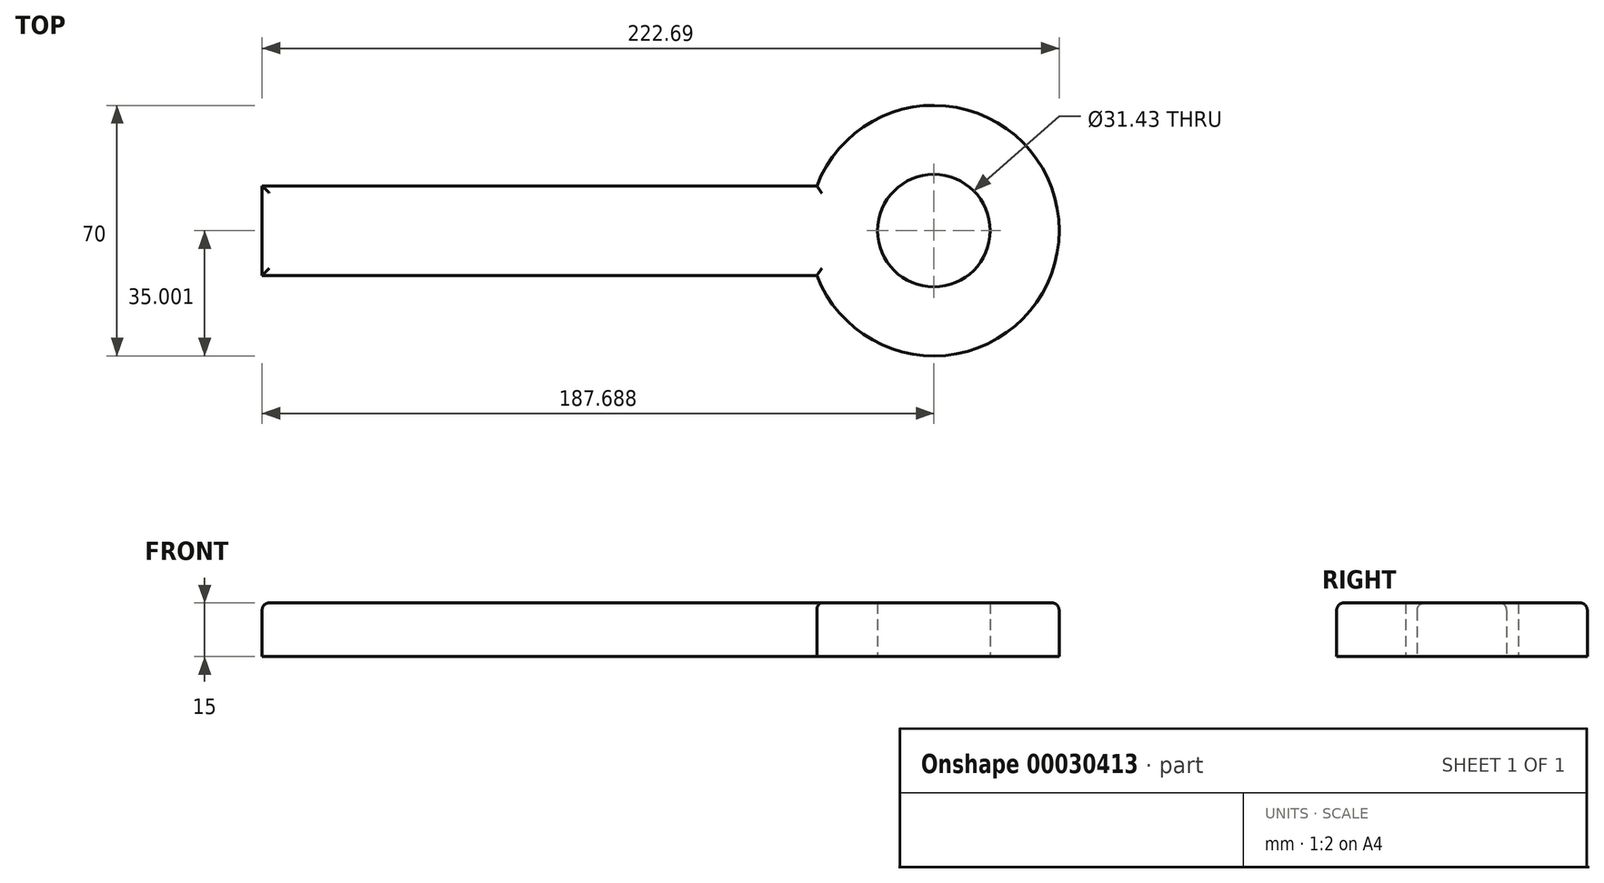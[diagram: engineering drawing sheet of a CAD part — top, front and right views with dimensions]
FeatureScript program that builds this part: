
annotation { "Feature Type Name" : "Feature", "Feature Type Description" : "" }
export const myFeature = defineFeature(function(context is Context, id is Id, definition is map)
    precondition{}
    {
        {
            var Q0;
            Q0=qCreatedBy(makeId("Top.planeOp"),FACE);
            var sketch = newSketch(context, id + "F0", { "sketchPlane" : qUnion([Q0])});
            skLineSegment(sketch, "E0.bottom", {"start": v(-82.43, 22.24) * mm, "end": v(72.57, 22.24) * mm});
            skLineSegment(sketch, "E0.top", {"start": v(-82.43, -2.76) * mm, "end": v(72.57, -2.76) * mm});
            skLineSegment(sketch, "E0.left", {"start": v(-82.43, 22.24) * mm, "end": v(-82.43, -2.76) * mm});
            skLineSegment(sketch, "E0.right", {"start": v(72.57, 22.24) * mm, "end": v(72.57, -2.76) * mm});
            skLineSegment(sketch, "E1.bottom", {"start": v(-82.43, -2.76) * mm, "end": v(-72.43, -2.76) * mm});
            skLineSegment(sketch, "E1.top", {"start": v(-82.43, -32.76) * mm, "end": v(-72.43, -32.76) * mm});
            skLineSegment(sketch, "E1.left", {"start": v(-82.43, -2.76) * mm, "end": v(-82.43, -32.76) * mm});
            skLineSegment(sketch, "E1.right", {"start": v(-72.43, -2.76) * mm, "end": v(-72.43, -32.76) * mm});
            skLineSegment(sketch, "E2.bottom", {"start": v(-62.43, -2.76) * mm, "end": v(-54.43, -2.76) * mm});
            skLineSegment(sketch, "E2.top", {"start": v(-62.43, -17.76) * mm, "end": v(-54.43, -17.76) * mm});
            skLineSegment(sketch, "E2.left", {"start": v(-62.43, -2.76) * mm, "end": v(-62.43, -17.76) * mm});
            skLineSegment(sketch, "E2.right", {"start": v(-54.43, -2.76) * mm, "end": v(-54.43, -17.76) * mm});
            skLineSegment(sketch, "E3", {"start": v(-44.43, -2.76) * mm, "end": v(-30.43, -2.76) * mm});
            skLineSegment(sketch, "E4", {"start": v(-30.43, -2.76) * mm, "end": v(-37.43, -16.03) * mm});
            skLineSegment(sketch, "E5", {"start": v(-44.43, -2.76) * mm, "end": v(-37.43, -16.03) * mm});
            skArc(sketch, "E6", {"start": v(72.57, -2.76) * mm, "mid": v(140.26, 9.74) * mm, "end": v(72.57, 22.24) * mm});
            skCircle(sketch, "E7", {"center": v(105.26, 9.74) * mm, "radius": 15.71 * mm});
            skLineSegment(sketch, "E8", {"start": v(-82.43, 9.74) * mm, "end": v(105.26, 9.74) * mm, "construction": true});
            skSolve(sketch);
        }
        {
            var Q0;
            Q0=makeQuery(id+"F0.imprint","IMPRINT",FACE,{"disambiguationData":[TD([[makeQuery(id+"F0.imprint","IMPRINT",EDGE,{"derivedFrom":sQuery(id+"F0.wireOp",EDGE,"E0.bottom")}),-1.0]])]});
            var Q1;
            Q1=makeQuery(id+"F0.imprint","IMPRINT",FACE,{"disambiguationData":[TD([[makeQuery(id+"F0.imprint","IMPRINT",EDGE,{"derivedFrom":sQuery(id+"F0.wireOp",EDGE,"E1.bottom")}),-1.0]])]});
            var Q2;
            Q2=makeQuery(id+"F0.imprint","IMPRINT",FACE,{"disambiguationData":[TD([[makeQuery(id+"F0.imprint","IMPRINT",EDGE,{"derivedFrom":sQuery(id+"F0.wireOp",EDGE,"E2.bottom")}),-1.0]])]});
            var Q3;
            Q3=makeQuery(id+"F0.imprint","IMPRINT",FACE,{"disambiguationData":[TD([[makeQuery(id+"F0.imprint","IMPRINT",EDGE,{"derivedFrom":sQuery(id+"F0.wireOp",EDGE,"E3")}),-1.0]])]});
            var Q4;
            Q4=makeQuery(id+"F0.imprint","IMPRINT",FACE,{"disambiguationData":[TD([[makeQuery(id+"F0.imprint","IMPRINT",EDGE,{"derivedFrom":sQuery(id+"F0.wireOp",EDGE,"E0.right")}),1.0]])]});
            extrude(context, id + "F1", {"entities" : qUnion([Q0, Q1, Q2, Q3, Q4]), "depth" : 15 * mm});
        }
        {
            var Q0;
            Q0=makeQuery(id+"F1.opExtrude","CAP_EDGE",EDGE,{"disambiguationData":[OSD([sQuery(id+"F0.wireOp",EDGE,"E0.left"),sQuery(id+"F0.wireOp",EDGE,"E1.left")])],"isStart":false});
            var Q1;
            Q1=makeQuery(id+"F1.opExtrude","CAP_EDGE",EDGE,{"disambiguationData":[OSD([sQuery(id+"F0.wireOp",EDGE,"E0.bottom")])],"isStart":false});
            var Q2;
            Q2=makeQuery(id+"F1.opExtrude","CAP_EDGE",EDGE,{"disambiguationData":[OSD([sQuery(id+"F0.wireOp",EDGE,"E1.right")])],"isStart":false});
            var Q3;
            Q3=makeQuery(id+"F1.opExtrude","CAP_EDGE",EDGE,{"disambiguationData":[OSD([sQuery(id+"F0.wireOp",EDGE,"E1.top")])],"isStart":false});
            var Q4;
            {var subQ0=sQuery(id+"F0.wireOp",EDGE,"E0.top");Q4=makeQuery(id+"F1.opExtrude","CAP_EDGE",EDGE,{"disambiguationData":[OSD([subQ0]),TDD([makeQuery(id+"F0.imprint","IMPRINT",EDGE,{"disambiguationData":[TD([[makeQuery(id+"F0.imprint","INTERSECT",VERTEX,{"derivedFrom":[subQ0,sQuery(id+"F0.wireOp",EDGE,"E1.bottom"),sQuery(id+"F0.wireOp",EDGE,"E1.right")]}),-1.0]])],"derivedFrom":subQ0})])],"isStart":false});}
            var Q5;
            Q5=makeQuery(id+"F1.opExtrude","CAP_EDGE",EDGE,{"disambiguationData":[OSD([sQuery(id+"F0.wireOp",EDGE,"E2.left")])],"isStart":false});
            var Q6;
            Q6=makeQuery(id+"F1.opExtrude","CAP_EDGE",EDGE,{"disambiguationData":[OSD([sQuery(id+"F0.wireOp",EDGE,"E2.top")])],"isStart":false});
            var Q7;
            {var subQ0=sQuery(id+"F0.wireOp",EDGE,"E0.top");Q7=makeQuery(id+"F1.opExtrude","CAP_EDGE",EDGE,{"disambiguationData":[OSD([subQ0]),TDD([makeQuery(id+"F0.imprint","IMPRINT",EDGE,{"disambiguationData":[TD([[makeQuery(id+"F0.imprint","INTERSECT",VERTEX,{"derivedFrom":[subQ0,sQuery(id+"F0.wireOp",EDGE,"E2.bottom"),sQuery(id+"F0.wireOp",EDGE,"E2.right")]}),-1.0]])],"derivedFrom":subQ0})])],"isStart":false});}
            var Q8;
            Q8=makeQuery(id+"F1.opExtrude","CAP_EDGE",EDGE,{"disambiguationData":[OSD([sQuery(id+"F0.wireOp",EDGE,"E2.right")])],"isStart":false});
            var Q9;
            Q9=makeQuery(id+"F1.opExtrude","CAP_EDGE",EDGE,{"disambiguationData":[OSD([sQuery(id+"F0.wireOp",EDGE,"E5")])],"isStart":false});
            var Q10;
            {var subQ0=sQuery(id+"F0.wireOp",EDGE,"E0.top");Q10=makeQuery(id+"F1.opExtrude","CAP_EDGE",EDGE,{"disambiguationData":[OSD([subQ0]),TDD([makeQuery(id+"F0.imprint","IMPRINT",EDGE,{"disambiguationData":[TD([[makeQuery(id+"F0.imprint","INTERSECT",VERTEX,{"derivedFrom":[subQ0,sQuery(id+"F0.wireOp",EDGE,"E0.right"),sQuery(id+"F0.wireOp",EDGE,"E6")]}),1.0]])],"derivedFrom":subQ0})])],"isStart":false});}
            var Q11;
            Q11=makeQuery(id+"F1.opExtrude","CAP_EDGE",EDGE,{"disambiguationData":[OSD([sQuery(id+"F0.wireOp",EDGE,"E4")])],"isStart":false});
            var Q12;
            Q12=makeQuery(id+"F1.opExtrude","CAP_EDGE",EDGE,{"disambiguationData":[OSD([sQuery(id+"F0.wireOp",EDGE,"E6")])],"isStart":false});
            fillet(context, id + "F2", {"entities" : qUnion([Q0, Q1, Q2, Q3, Q4, Q5, Q6, Q7, Q8, Q9, Q10, Q11, Q12]), "radius" : 2 * mm, "tangentPropagation" : true, "allowEdgeOverflow" : false});
        }
    });
